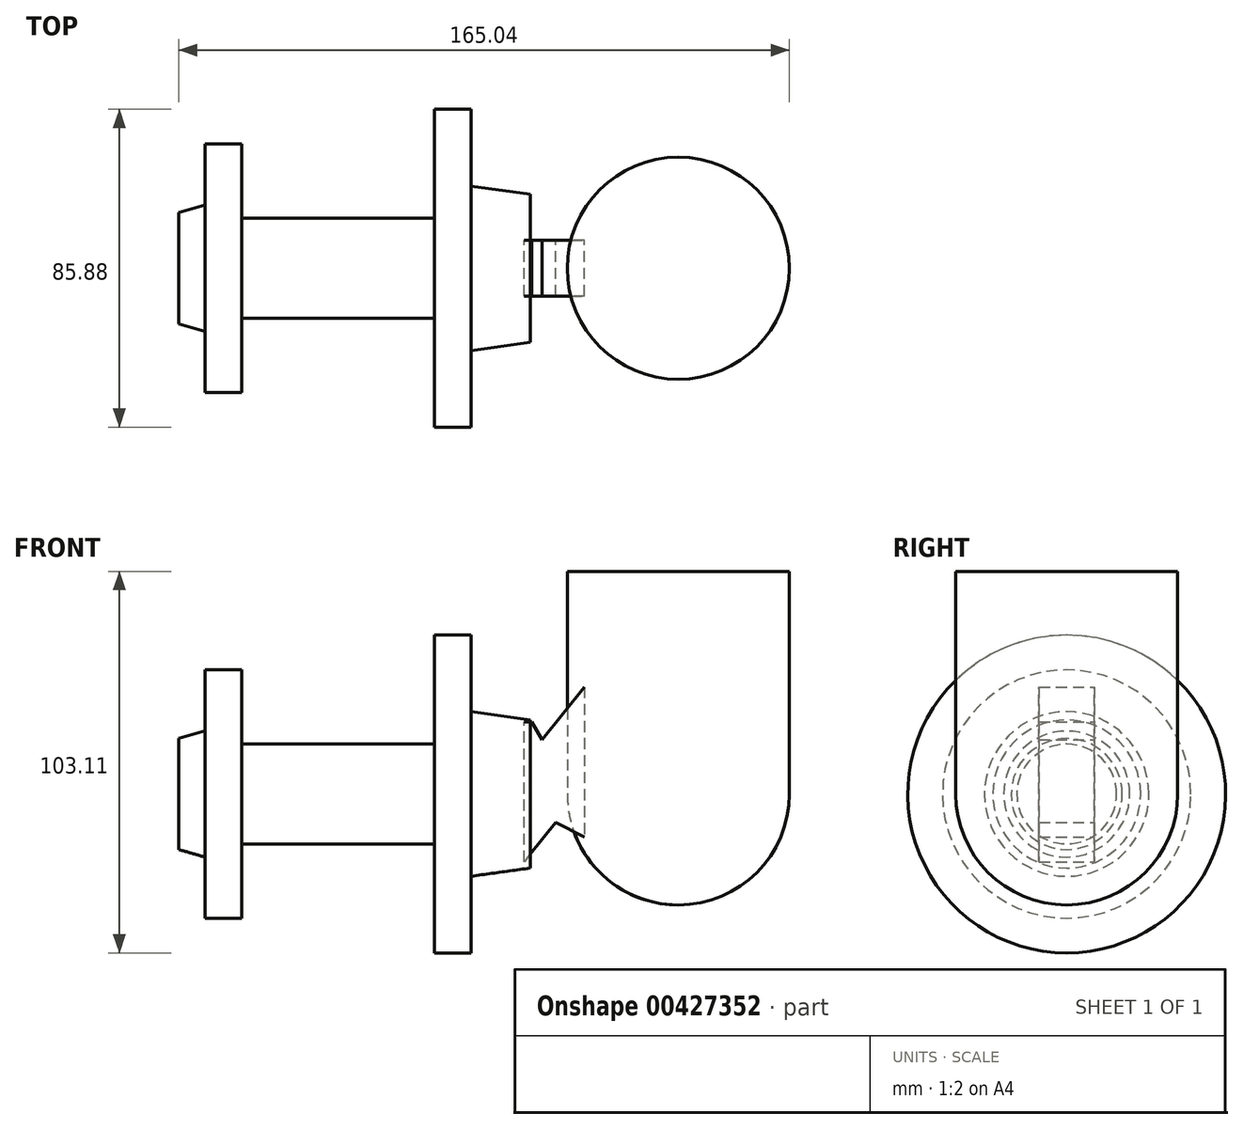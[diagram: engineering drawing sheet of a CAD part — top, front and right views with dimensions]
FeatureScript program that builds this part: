
annotation { "Feature Type Name" : "Feature", "Feature Type Description" : "" }
export const myFeature = defineFeature(function(context is Context, id is Id, definition is map)
    precondition{}
    {
        {
            var Q0;
            Q0=qCreatedBy(makeId("Front.planeOp"),FACE);
            var sketch = newSketch(context, id + "F0", { "sketchPlane" : qUnion([Q0])});
            skLineSegment(sketch, "E0", {"start": v(-50.04, 0) * mm, "end": v(-50.04, -15) * mm});
            skLineSegment(sketch, "E1", {"start": v(-50.04, -15) * mm, "end": v(-42.93, -17.03) * mm});
            skLineSegment(sketch, "E2", {"start": v(-42.93, -17.03) * mm, "end": v(-42.93, -33.54) * mm});
            skLineSegment(sketch, "E3", {"start": v(-42.93, -33.54) * mm, "end": v(-32.93, -33.54) * mm});
            skLineSegment(sketch, "E4", {"start": v(-32.93, -33.54) * mm, "end": v(-32.93, -13.48) * mm});
            skLineSegment(sketch, "E5", {"start": v(-32.93, -13.48) * mm, "end": v(19.07, -13.48) * mm});
            skLineSegment(sketch, "E6", {"start": v(19.07, -13.48) * mm, "end": v(19.07, -42.94) * mm});
            skLineSegment(sketch, "E7", {"start": v(19.07, -42.94) * mm, "end": v(29.07, -42.94) * mm});
            skLineSegment(sketch, "E8", {"start": v(29.07, -42.94) * mm, "end": v(29.07, -22.23) * mm});
            skLineSegment(sketch, "E9", {"start": v(29.07, -22.23) * mm, "end": v(44.96, -20) * mm});
            skLineSegment(sketch, "E10", {"start": v(44.96, -20) * mm, "end": v(44.96, 0) * mm});
            skLineSegment(sketch, "E11", {"start": v(44.96, 0) * mm, "end": v(-50.04, 0) * mm});
            skSolve(sketch);
        }
        {
            var Q0;
            Q0=makeQuery(id+"F0.imprint","IMPRINT",FACE,{"disambiguationData":[TD([[makeQuery(id+"F0.imprint","IMPRINT",EDGE,{"derivedFrom":sQuery(id+"F0.wireOp",EDGE,"E0")}),1.0]])]});
            var Q1;
            Q1=sQuery(id+"F0.wireOp",EDGE,"E11");
            revolve(context, id + "F1", {"entities" : qUnion([Q0]), "axis" : qUnion([Q1]), "revolveType" : RevolveType.FULL});
        }
        {
            var Q0;
            Q0=qCreatedBy(makeId("Front.planeOp"),FACE);
            var sketch = newSketch(context, id + "F2", { "sketchPlane" : qUnion([Q0])});
            skLineSegment(sketch, "E12", {"start": v(55, 60.17) * mm, "end": v(55, 0) * mm});
            skLineSegment(sketch, "E13", {"start": v(85, -30) * mm, "end": v(85, 60) * mm});
            skLineSegment(sketch, "E14", {"start": v(85, 60) * mm, "end": v(55, 60.17) * mm});
            skArc(sketch, "E15", {"start": v(55, 0) * mm, "mid": v(63.79, -21.21) * mm, "end": v(85, -30) * mm});
            skSolve(sketch);
        }
        {
            var Q0;
            Q0 = qSketchRegion(id + "F2", true);
            var Q1;
            Q1=sQuery(id+"F2.wireOp",EDGE,"E13");
            revolve(context, id + "F3", {"entities" : qUnion([Q0]), "axis" : qUnion([Q1]), "revolveType" : RevolveType.FULL});
        }
        {
            var Q0;
            Q0=qCreatedBy(makeId("Front.planeOp"),FACE);
            var sketch = newSketch(context, id + "F4", { "sketchPlane" : qUnion([Q0])});
            skLineSegment(sketch, "E16", {"start": v(45.37, 19.49) * mm, "end": v(48.13, 14.64) * mm});
            skLineSegment(sketch, "E17", {"start": v(48.13, 14.64) * mm, "end": v(59.66, 28.94) * mm});
            skLineSegment(sketch, "E18", {"start": v(59.66, 28.94) * mm, "end": v(59.66, -11.65) * mm});
            skLineSegment(sketch, "E19", {"start": v(59.66, -11.65) * mm, "end": v(51.82, -7.73) * mm});
            skLineSegment(sketch, "E20", {"start": v(51.82, -7.73) * mm, "end": v(43.3, -18.3) * mm});
            skLineSegment(sketch, "E21", {"start": v(43.3, -18.3) * mm, "end": v(43.3, 19.49) * mm});
            skLineSegment(sketch, "E22", {"start": v(43.3, 19.49) * mm, "end": v(45.37, 19.49) * mm});
            skSolve(sketch);
        }
        {
            var Q0;
            Q0=makeQuery(id+"F4.imprint","IMPRINT",FACE,{"disambiguationData":[TD([[makeQuery(id+"F4.imprint","IMPRINT",EDGE,{"derivedFrom":sQuery(id+"F4.wireOp",EDGE,"E16")}),-1.0]])]});
            extrude(context, id + "F5", {"entities" : qUnion([Q0]), "endBound" : BoundingType.SYMMETRIC, "depth" : 15 * mm});
        }
    });
